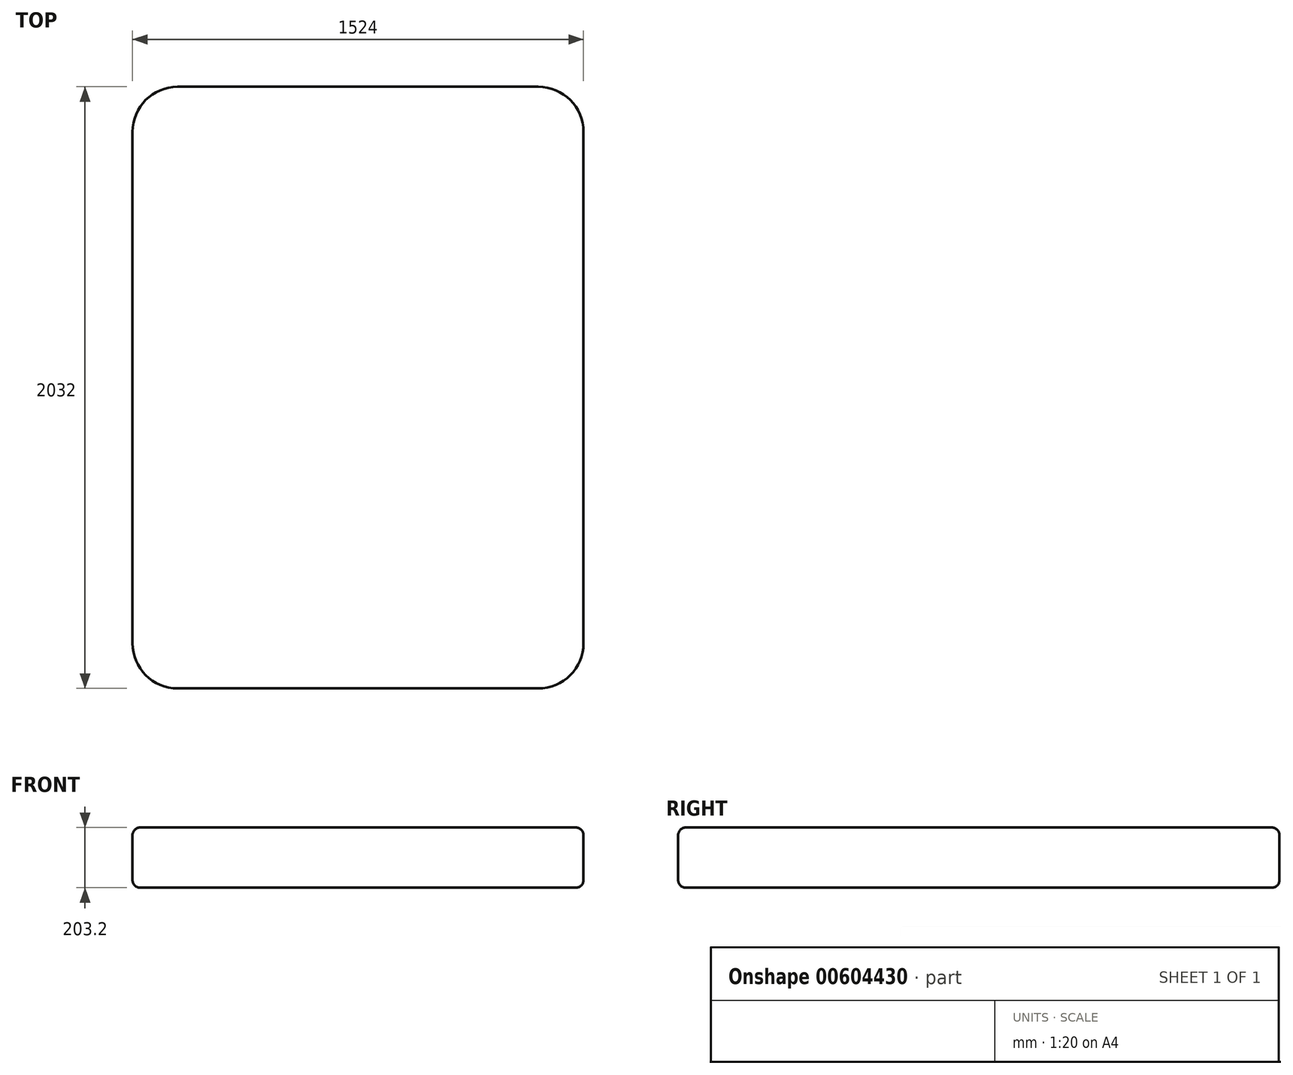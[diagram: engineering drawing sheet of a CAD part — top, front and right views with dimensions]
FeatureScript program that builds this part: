
annotation { "Feature Type Name" : "Feature", "Feature Type Description" : "" }
export const myFeature = defineFeature(function(context is Context, id is Id, definition is map)
    precondition{}
    {
        {
            var Q0;
            Q0=qCreatedBy(makeId("Top.planeOp"),FACE);
            var sketch = newSketch(context, id + "F0", { "sketchPlane" : qUnion([Q0])});
            skLineSegment(sketch, "E0.bottom", {"start": v(762, -1016) * mm, "end": v(-762, -1016) * mm});
            skLineSegment(sketch, "E0.top", {"start": v(762, 1016) * mm, "end": v(-762, 1016) * mm});
            skLineSegment(sketch, "E0.left", {"start": v(762, -1016) * mm, "end": v(762, 1016) * mm});
            skLineSegment(sketch, "E0.right", {"start": v(-762, -1016) * mm, "end": v(-762, 1016) * mm});
            skPoint(sketch, "E0.middle", {"position": v(0, 0) * mm});
            skSolve(sketch);
        }
        {
            var Q0;
            Q0=makeQuery(id+"F0.imprint","IMPRINT",FACE,{"disambiguationData":[TD([[makeQuery(id+"F0.imprint","IMPRINT",EDGE,{"derivedFrom":sQuery(id+"F0.wireOp",EDGE,"E0.bottom")}),-1.0]])]});
            extrude(context, id + "F1", {"entities" : qUnion([Q0]), "depth" : 203.2 * mm, "offsetDistance" : 25.4 * mm});
        }
        {
            var Q0;
            Q0=makeQuery(id+"F1.opExtrude","SWEPT_EDGE",EDGE,{"disambiguationData":[OSD([sQuery(id+"F0.wireOp",EDGE,"E0.bottom"),sQuery(id+"F0.wireOp",EDGE,"E0.right")])]});
            var Q1;
            Q1=makeQuery(id+"F1.opExtrude","SWEPT_EDGE",EDGE,{"disambiguationData":[OSD([sQuery(id+"F0.wireOp",EDGE,"E0.bottom"),sQuery(id+"F0.wireOp",EDGE,"E0.left")])]});
            var Q2;
            Q2=makeQuery(id+"F1.opExtrude","SWEPT_EDGE",EDGE,{"disambiguationData":[OSD([sQuery(id+"F0.wireOp",EDGE,"E0.top"),sQuery(id+"F0.wireOp",EDGE,"E0.left")])]});
            var Q3;
            Q3=makeQuery(id+"F1.opExtrude","SWEPT_EDGE",EDGE,{"disambiguationData":[OSD([sQuery(id+"F0.wireOp",EDGE,"E0.top"),sQuery(id+"F0.wireOp",EDGE,"E0.right")])]});
            fillet(context, id + "F2", {"entities" : qUnion([Q0, Q1, Q2, Q3]), "radius" : 152.4 * mm, "tangentPropagation" : true, "allowEdgeOverflow" : false});
        }
        {
            var Q0;
            Q0=makeQuery(id+"F1.opExtrude","CAP_FACE",FACE,{"disambiguationData":[OSD([sQuery(id+"F0.wireOp",EDGE,"E0.bottom"),sQuery(id+"F0.wireOp",EDGE,"E0.top"),sQuery(id+"F0.wireOp",EDGE,"E0.left"),sQuery(id+"F0.wireOp",EDGE,"E0.right")])],"isStart":false});
            var Q1;
            Q1=makeQuery(id+"F1.opExtrude","CAP_FACE",FACE,{"disambiguationData":[OSD([sQuery(id+"F0.wireOp",EDGE,"E0.bottom"),sQuery(id+"F0.wireOp",EDGE,"E0.top"),sQuery(id+"F0.wireOp",EDGE,"E0.left"),sQuery(id+"F0.wireOp",EDGE,"E0.right")])],"isStart":true});
            fillet(context, id + "F3", {"entities" : qUnion([Q0, Q1]), "radius" : 25.4 * mm, "tangentPropagation" : true, "allowEdgeOverflow" : false});
        }
    });
